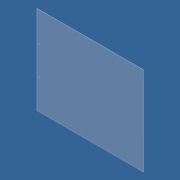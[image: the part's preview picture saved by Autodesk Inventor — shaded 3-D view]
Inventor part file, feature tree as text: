
AUTODESK INVENTOR PART (.ipt)
format: ipt  version: 2012 (Build 160160000, 160)  size: 74,752 bytes
history: native  units: in
note: dims shown in document units (in); Inventor stores cm internally (conversion verified against a paired STEP export)
features: extrude x1, hole x1, pattern_linear x1, sketch x1
ambient origin geometry x8: Origin, YZ Plane, XZ Plane, XY Plane, X Axis, Y Axis, Z Axis, Center Point
bodies: Solid1 (feature_tree)
feature tree (4):
  extrude  "Extrusion1"  Depth=50.0in
  hole  "Hole1"  [1 undecoded]
  pattern_linear  "Rectangular Pattern1"  Count1=2 Spacing1=13.5in
  sketch  "Sketch1"  dims[d0=41.5in d1=50.0in d2=0.25in d3=0.0in d4=1.0in d5=14.0in d6=0.5in d7=0.75in d8=0.375in d9=0.25in d10=0.5635in d11=1.0in d12=0.8108in d13=0.7874in d15=13.5in]
note: 1 required parameter value undecoded (feature->parameter linkage not recoverable at this tier; creation-order binding heuristic only, values carry confidence <= 0.55)
